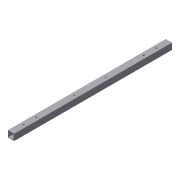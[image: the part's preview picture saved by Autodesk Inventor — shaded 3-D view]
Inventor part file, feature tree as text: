
AUTODESK INVENTOR PART (.ipt)
format: ipt  version: 2012 (Build 160160000, 160)  size: 109,568 bytes
history: native  units: in
note: dims shown in document units (in); Inventor stores cm internally (conversion verified against a paired STEP export)
features: extrude x3, sketch x3, shell x1
ambient origin geometry x8: Origin, YZ Plane, XZ Plane, XY Plane, X Axis, Y Axis, Z Axis, Center Point
bodies: Solid1 (feature_tree)
feature tree (7):
  extrude  "Extrusion1"  Depth=1.0in
  shell  "Shell1"  Thickness=25.0in
  extrude  "Extrusion2"  Depth=2.0in
  extrude  "Extrusion3"  Depth=0.5in
  sketch  "Sketch1"  dims[d0=1.0in d1=1.0in d2=25.0in d3=0.0in]
  sketch  "Sketch2"  dims[d4=0.125in d7=2.0in]
  sketch  "Sketch3"  dims[d8=2.0in d9=0.5in d10=0.5in d11=0.25in d12=0.25in d13=0.5in d14=0.5in d15=2.0in d16=2.0in d17=0.25in d18=0.25in d19=35.0in d20=0.0in d21=0.1875in d22=0.1875in d23=5.0in d24=10.0in d25=35.0in d26=0.0in]
